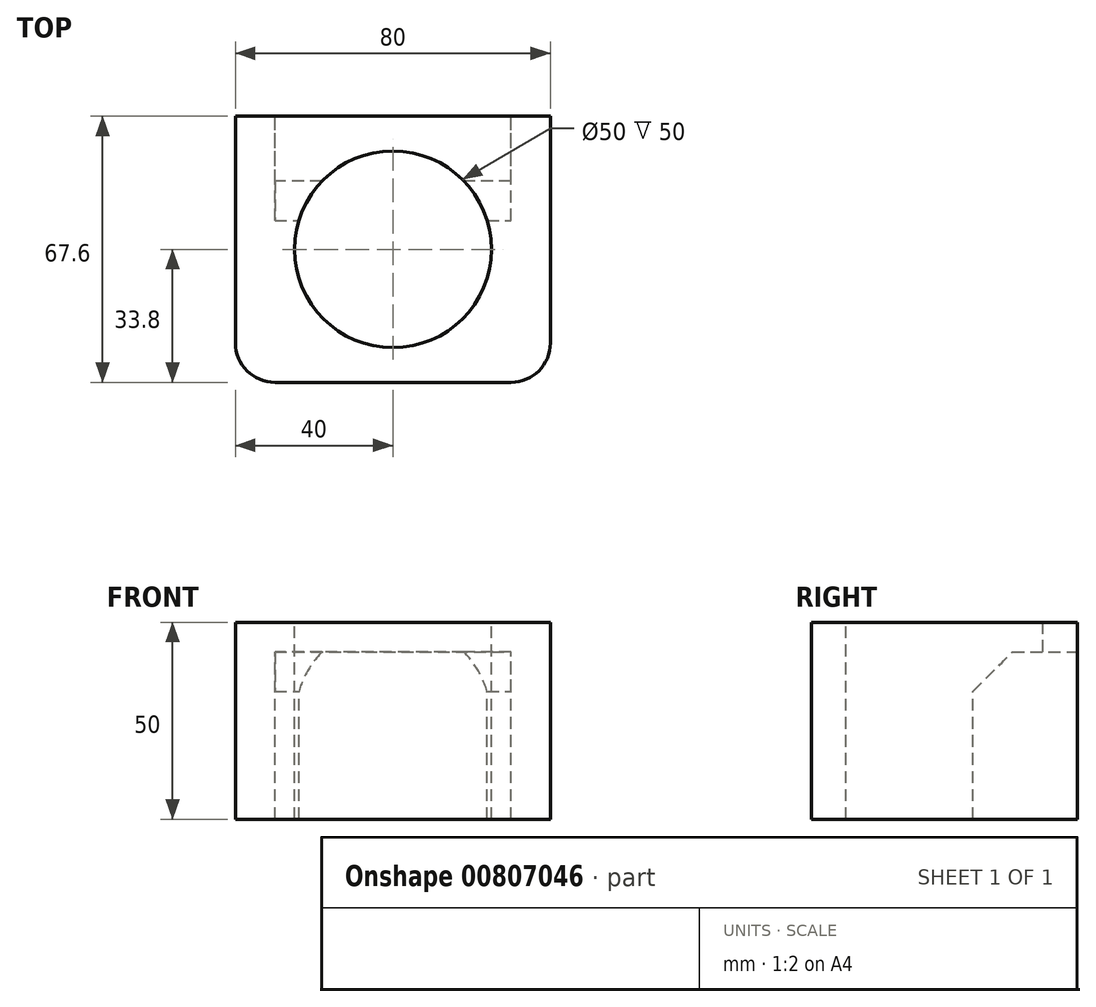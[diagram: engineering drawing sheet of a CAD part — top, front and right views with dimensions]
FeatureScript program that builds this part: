
annotation { "Feature Type Name" : "Feature", "Feature Type Description" : "" }
export const myFeature = defineFeature(function(context is Context, id is Id, definition is map)
    precondition{}
    {
        {
            var Q0;
            Q0=qCreatedBy(makeId("Front.planeOp"),FACE);
            var sketch = newSketch(context, id + "F0", { "sketchPlane" : qUnion([Q0])});
            skLineSegment(sketch, "E0.bottom", {"start": v(40, -25) * mm, "end": v(-40, -25) * mm});
            skLineSegment(sketch, "E0.top", {"start": v(40, 25) * mm, "end": v(-40, 25) * mm});
            skLineSegment(sketch, "E0.left", {"start": v(40, -25) * mm, "end": v(40, 25) * mm});
            skLineSegment(sketch, "E0.right", {"start": v(-40, -25) * mm, "end": v(-40, 25) * mm});
            skPoint(sketch, "E0.middle", {"position": v(0, 0) * mm});
            skSolve(sketch);
        }
        {
            var Q0;
            Q0=makeQuery(id+"F0.imprint","IMPRINT",FACE,{"disambiguationData":[TD([[makeQuery(id+"F0.imprint","IMPRINT",EDGE,{"derivedFrom":sQuery(id+"F0.wireOp",EDGE,"E0.bottom")}),-1.0]])]});
            extrude(context, id + "F1", {"entities" : qUnion([Q0]), "endBound" : BoundingType.SYMMETRIC, "depth" : 67.6 * mm, "offsetDistance" : 25 * mm});
        }
        {
            var Q0;
            Q0=makeQuery(id+"F1.opExtrude","SWEPT_FACE",FACE,{"disambiguationData":[OSD([sQuery(id+"F0.wireOp",EDGE,"E0.top")])]});
            var sketch = newSketch(context, id + "F2", { "sketchPlane" : qUnion([Q0])});
            skCircle(sketch, "E1", {"center": v(0, 0) * mm, "radius": 25 * mm});
            skSolve(sketch);
        }
        {
            var Q0;
            Q0=makeQuery(id+"F2.imprint","IMPRINT",FACE,{"disambiguationData":[TD([[makeQuery(id+"F2.imprint","IMPRINT",EDGE,{"derivedFrom":sQuery(id+"F2.wireOp",EDGE,"E1")}),1.0]])]});
            extrude(context, id + "F3", {"entities" : qUnion([Q0]), "operationType" : NewBodyOperationType.REMOVE, "oppositeDirection" : true, "depth" : 104.1 * mm, "offsetDistance" : 25 * mm});
        }
        {
            var Q0;
            Q0=makeQuery(id+"F1.opExtrude","CAP_EDGE",EDGE,{"disambiguationData":[OSD([sQuery(id+"F0.wireOp",EDGE,"E0.left")])],"isStart":false});
            var Q1;
            Q1=makeQuery(id+"F1.opExtrude","CAP_EDGE",EDGE,{"disambiguationData":[OSD([sQuery(id+"F0.wireOp",EDGE,"E0.right")])],"isStart":false});
            fillet(context, id + "F4", {"entities" : qUnion([Q0, Q1]), "radius" : 10 * mm, "tangentPropagation" : true, "allowEdgeOverflow" : false});
        }
        {
            var Q0;
            Q0=makeQuery(id+"F1.opExtrude","CAP_FACE",FACE,{"disambiguationData":[OSD([sQuery(id+"F0.wireOp",EDGE,"E0.bottom"),sQuery(id+"F0.wireOp",EDGE,"E0.top"),sQuery(id+"F0.wireOp",EDGE,"E0.left"),sQuery(id+"F0.wireOp",EDGE,"E0.right")])],"isStart":true});
            var sketch = newSketch(context, id + "F5", { "sketchPlane" : qUnion([Q0])});
            skLineSegment(sketch, "E2.bottom", {"start": v(30, -32.5) * mm, "end": v(-30, -32.5) * mm});
            skLineSegment(sketch, "E2.top", {"start": v(30, 17.5) * mm, "end": v(-30, 17.5) * mm});
            skLineSegment(sketch, "E2.left", {"start": v(30, -32.5) * mm, "end": v(30, 17.5) * mm});
            skLineSegment(sketch, "E2.right", {"start": v(-30, -32.5) * mm, "end": v(-30, 17.5) * mm});
            skSolve(sketch);
        }
        {
            var Q0;
            {var subQ0=sQuery(id+"F5.wireOp",EDGE,"E2.top");Q0=makeQuery(id+"F5.imprint","IMPRINT",FACE,{"disambiguationData":[TD([[makeQuery(id+"F5.imprint","IMPRINT",EDGE,{"derivedFrom":subQ0}),1.0]])]});}
            var Q1;
            {var subQ0=sQuery(id+"F5.wireOp",EDGE,"E2.bottom");Q1=makeQuery(id+"F5.imprint","IMPRINT",FACE,{"disambiguationData":[TD([[makeQuery(id+"F5.imprint","IMPRINT",EDGE,{"derivedFrom":subQ0}),-1.0]])]});}
            extrude(context, id + "F6", {"entities" : qUnion([Q0, Q1]), "operationType" : NewBodyOperationType.REMOVE, "oppositeDirection" : true, "depth" : 26.5 * mm, "offsetDistance" : 25 * mm});
        }
        {
            var Q0;
            {var subQ0=sQuery(id+"F5.wireOp",EDGE,"E2.right");var subQ1=sQuery(id+"F5.wireOp",EDGE,"E2.top");Q0=makeQuery(id+"F6.boolean.opBoolean","COPY",EDGE,{"disambiguationData":[TD([makeQuery(id+"F6.opExtrude","SWEPT_FACE",FACE,{"disambiguationData":[OSD([subQ0])]})])],"derivedFrom":makeQuery(id+"F6.opExtrude","CAP_EDGE",EDGE,{"disambiguationData":[OSD([subQ1])],"isStart":false})});}
            var Q1;
            {var subQ0=sQuery(id+"F5.wireOp",EDGE,"E2.left");var subQ1=sQuery(id+"F5.wireOp",EDGE,"E2.top");Q1=makeQuery(id+"F6.boolean.opBoolean","COPY",EDGE,{"disambiguationData":[TD([makeQuery(id+"F6.opExtrude","SWEPT_FACE",FACE,{"disambiguationData":[OSD([subQ0])]})])],"derivedFrom":makeQuery(id+"F6.opExtrude","CAP_EDGE",EDGE,{"disambiguationData":[OSD([subQ1])],"isStart":false})});}
            chamfer(context, id + "F7", {"entities" : qUnion([Q0, Q1]), "width" : 10 * mm, "tangentPropagation" : true});
        }
    });
